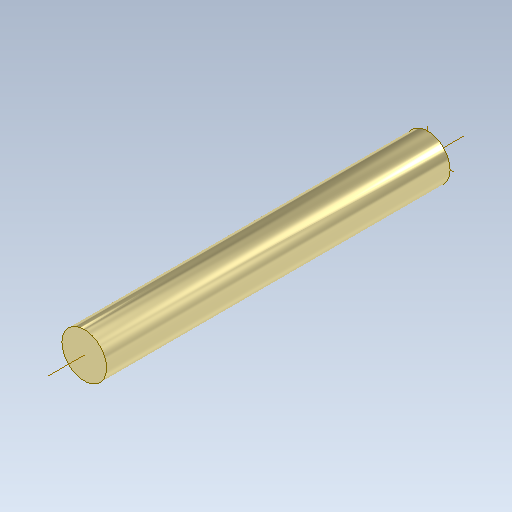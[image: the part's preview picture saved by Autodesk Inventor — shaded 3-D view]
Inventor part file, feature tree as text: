
AUTODESK INVENTOR PART (.ipt)
format: ipt  version: 2021.1 (Build 251245000, 245)  size: 101,376 bytes
history: native  units: in
note: dims shown in document units (in); Inventor stores cm internally (conversion verified against a paired STEP export)
features: extrude x1, sketch x1
ambient origin geometry x8: Origin, YZ Plane, XZ Plane, XY Plane, X Axis, Y Axis, Z Axis, Center Point
bodies: Solid1 (feature_tree)
feature tree (2):
  extrude  "Extrusion1"  Depth=3.937in TaperAngle=0.0deg
  sketch  "Sketch1"  dims[d0=0.5118in d1=3.937in d2=0.0in]
